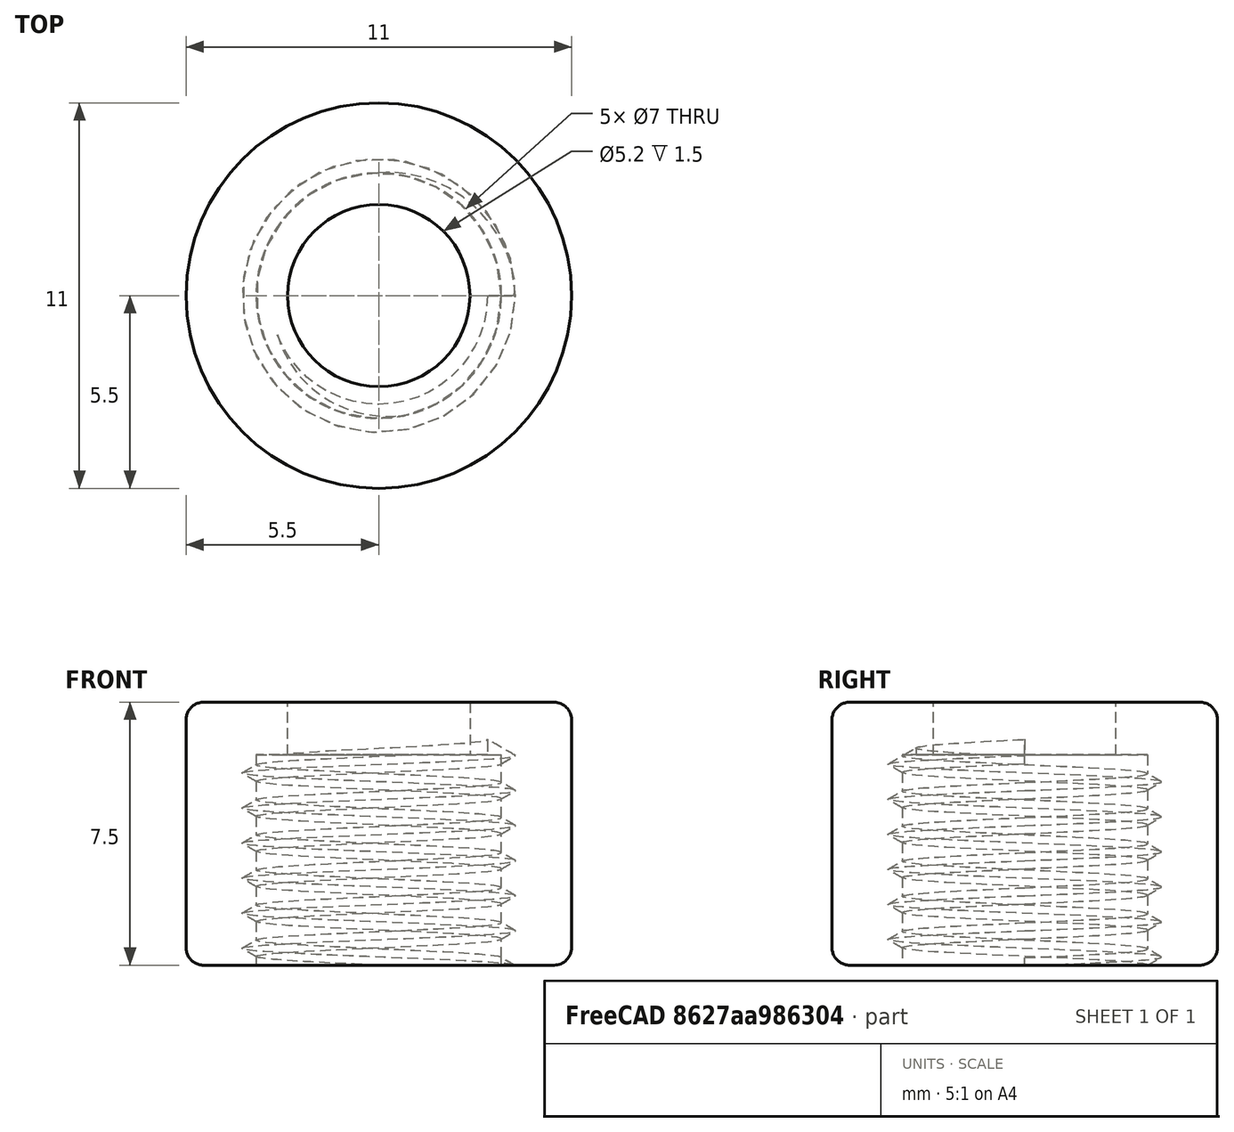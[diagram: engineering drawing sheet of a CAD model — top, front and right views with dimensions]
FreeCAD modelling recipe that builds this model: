
FCSTD DOCUMENT  (FreeCAD 0.19R24291 (Git))
Label: soldernut
License: All rights reserved
LicenseURL: http://en.wikipedia.org/wiki/All_rights_reserved
objects: TechDraw::DrawViewDimension×7, Sketcher::SketchObject×4, TechDraw::DrawProjGroupItem×4, Part::Extrusion×3, Part::Cut×3, Part::Fillet×2, Part::Helix×1, PartDesign::Body×1, Part::Sweep×1, TechDraw::DrawSVGTemplate×1, TechDraw::DrawProjGroup×1, TechDraw::DrawViewSection×1, TechDraw::DrawPage×1
note: 15 computed .brp shape members not serialized (recipe doc carries the construction recipe); baked Part::Feature solids carry a one-line shape summary decoded from their .brp

FEATURE [Sketcher::SketchObject] Sketch
  FullyConstrained = true
  Placement = pos=(0,0,0) rot=(1,0,0;3.14159rad)
  sketch-geometry (1):
    g0: Circle CenterX=0 CenterY=0 CenterZ=0 NormalX=0 NormalY=0 NormalZ=1 AngleXU=0 Radius=5.5
  constraints (2):
    c: Coincident(g0,g-1)
    c: Radius(g0) = 5.5  'внешний контур'
FEATURE [Part::Extrusion] Extrude
  Base = -> Sketch
  Dir = (0,0,-1)
  DirMode = 2
  FaceMakerClass = Part::FaceMakerBullseye
  LengthFwd = 7.5
  LengthRev = 0
  Solid = true
  Symmetric = false
FEATURE [Sketcher::SketchObject] Sketch001
  FullyConstrained = true
  MapMode = 5
  Placement = pos=(0,0,-7.5) rot=(1,0,0;3.14159rad)
  Support = -> [Extrude]
  sketch-geometry (1):
    g0: Circle CenterX=0 CenterY=0 CenterZ=0 NormalX=0 NormalY=0 NormalZ=1 AngleXU=0 Radius=3.5
  constraints (2):
    c: Coincident(g0,g-1)
    c: Radius(g0) = 3.5  'Внутренний больший радиус'
FEATURE [Part::Extrusion] Extrude001
  Base = -> Sketch001
  Dir = (0,0,-1)
  DirMode = 2
  FaceMakerClass = Part::FaceMakerBullseye
  LengthFwd = -6
  LengthRev = 0
  Solid = true
  Symmetric = false
FEATURE [Part::Cut] Cut
  Base = -> Extrude
  Tool = -> Extrude001
FEATURE [Sketcher::SketchObject] Sketch002
  FullyConstrained = true
  MapMode = 5
  Support = -> [Cut]
  sketch-geometry (1):
    g0: Circle CenterX=0 CenterY=0 CenterZ=0 NormalX=0 NormalY=0 NormalZ=1 AngleXU=0 Radius=2.6
  constraints (2):
    c: Coincident(g0,g-1)
    c: Radius(g0) = 2.6
FEATURE [Part::Extrusion] Extrude002
  Base = -> Sketch002
  Dir = (0,0,1)
  DirMode = 2
  FaceMakerClass = Part::FaceMakerBullseye
  LengthFwd = -8
  LengthRev = 0
  Solid = true
  Symmetric = false
FEATURE [Part::Cut] Cut001
  Base = -> Cut
  Tool = -> Extrude002
FEATURE [Part::Fillet] Fillet
  Base = -> Cut001
  Edges = 1 edges r=0.5: [Edge2]
FEATURE [Part::Fillet] Fillet001
  Base = -> Fillet
  Edges = 1 edges r=0.5: [Edge2]
FEATURE [Part::Helix] Helix  label="Спираль"
  Angle = 0
  AttacherType = Attacher::AttachEngine3D
  Height = 6
  LocalCoord = 0
  Pitch = 1
  Placement = pos=(0,0,-7.5) rot=(0,0,1;0rad)
  Radius = 3.5
  Style = 1
FEATURE [Sketcher::SketchObject] Sketch003
  FullyConstrained = true
  MapMode = 5
  Placement = pos=(0,0,0) rot=(1,0,0;1.5708rad)
  Support = -> [XZ_Plane]
  sketch-geometry (3):
    g0: LineSegment StartX=3.9 StartY=-7.52 StartZ=0 EndX=3.1 EndY=-7.05812 EndZ=0
    g1: LineSegment StartX=3.1 StartY=-7.05812 StartZ=0 EndX=3.1 EndY=-7.98188 EndZ=0
    g2: LineSegment StartX=3.1 StartY=-7.98188 StartZ=0 EndX=3.9 EndY=-7.52 EndZ=0
  constraints (9):
    c: Coincident(g0,g1)
    c: Vertical(g1)
    c: Coincident(g1,g2)
    c: Coincident(g2,g0)
    c: Equal(g0,g2)
    c: Angle(g0,g2) = 1.0472
    c: DistanceX(g-1,g0) = 3.9
    c: DistanceY(g0,g-1) = 7.52
    c: DistanceX(g-1,g1) = 3.1
FEATURE [PartDesign::Body] Body
  Group = -> [Sketch003]
  Origin = -> Origin
FEATURE [Part::Sweep] Sweep
  Frenet = true
  Sections = -> [Sketch003]
  Solid = true
  Spine = -> Helix [Edge1,Edge2,Edge3,Edge4,Edge5,Edge6]
  Transition = 1
FEATURE [Part::Cut] Cut002
  Base = -> Fillet001
  Tool = -> Sweep
FEATURE [TechDraw::DrawSVGTemplate] Template
  Height = 297
  Orientation = 1
  Width = 420
FEATURE [TechDraw::DrawProjGroupItem] ProjItem  label="Front"
  CoarseView = false
  Direction = (0,-1,0)
  Focus = 100
  HardHidden = false
  IsoCount = 0
  IsoHidden = false
  IsoVisible = false
  LockPosition = true
  Perspective = false
  Rotation = 0
  RotationVector = (1,0,0)
  Scale = 6
  ScaleType = 2
  SeamHidden = false
  SeamVisible = true
  SmoothHidden = false
  SmoothVisible = true
  Source = -> [Cut002]
  Type = 0
  X = 0
  XDirection = (1,0,0)
  Y = 0
FEATURE [TechDraw::DrawProjGroupItem] ProjItem001  label="Bottom"
  CoarseView = false
  Direction = (0,0,-1)
  Focus = 100
  HardHidden = false
  IsoCount = 0
  IsoHidden = false
  IsoVisible = false
  LockPosition = false
  Perspective = false
  Rotation = 0
  RotationVector = (1,0,0)
  Scale = 6
  ScaleType = 2
  SeamHidden = false
  SeamVisible = true
  SmoothHidden = false
  SmoothVisible = true
  Source = -> [Cut002]
  Type = 5
  X = 0
  XDirection = (1,0,0)
  Y = 85.9201
FEATURE [TechDraw::DrawProjGroupItem] ProjItem002  label="Top"
  CoarseView = false
  Direction = (0,0,1)
  Focus = 100
  HardHidden = false
  IsoCount = 0
  IsoHidden = false
  IsoVisible = false
  LockPosition = false
  Perspective = false
  Rotation = 0
  RotationVector = (1,0,0)
  Scale = 6
  ScaleType = 2
  SeamHidden = false
  SeamVisible = true
  SmoothHidden = false
  SmoothVisible = true
  Source = -> [Cut002]
  Type = 4
  X = 0
  XDirection = (1,0,0)
  Y = -89.9779
FEATURE [TechDraw::DrawProjGroupItem] ProjItem003  label="FrontBottomLeft"
  CoarseView = false
  Direction = (-0.57735,-0.57735,-0.57735)
  Focus = 100
  HardHidden = false
  IsoCount = 0
  IsoHidden = false
  IsoVisible = false
  LockPosition = false
  Perspective = false
  Rotation = 0
  RotationVector = (1,0,0)
  Scale = 6
  ScaleType = 2
  SeamHidden = false
  SeamVisible = true
  SmoothHidden = false
  SmoothVisible = true
  Source = -> [Cut002]
  Type = 8
  X = 84.7919
  XDirection = (0.707107,-0.707107,0)
  Y = 89.4829
FEATURE [TechDraw::DrawProjGroup] ProjGroup
  Anchor = -> ProjItem
  AutoDistribute = true
  LockPosition = false
  ProjectionType = 0
  Rotation = 0
  Scale = 6
  ScaleType = 2
  Source = -> [Cut002]
  Views = -> [ProjItem,ProjItem001,ProjItem002,ProjItem003]
  X = 72.5645
  Y = 156.996
  spacingX = 15
  spacingY = 15
FEATURE [TechDraw::DrawViewSection] SectionView  label="Section  - "
  BaseView = -> ProjItem
  CoarseView = false
  CutSurfaceDisplay = 2
  Direction = (-1,0,0)
  FileGeomPattern = C:/Program Files/FreeCAD 0.19/data/Mod/TechDraw/PAT/FCPAT.pat
  FileHatchPattern = C:/Program Files/FreeCAD 0.19/data/Mod/TechDraw/Patterns/simple.svg
  Focus = 100
  FuseBeforeCut = false
  HardHidden = false
  HatchScale = 1
  IsoCount = 0
  IsoHidden = false
  IsoVisible = false
  LockPosition = false
  NameGeomPattern = Diamond
  Perspective = false
  Rotation = 0
  Scale = 15
  ScaleType = 0
  SeamHidden = false
  SeamVisible = true
  SectionDirection = 0
  SectionNormal = (-1,0,0)
  SectionOrigin = (-0.16,0,-3.99)
  SmoothHidden = false
  SmoothVisible = true
  Source = -> [Cut002]
  X = 282.206
  XDirection = (0,-1,0)
  Y = 97.5996
FEATURE [TechDraw::DrawViewDimension] Dimension
  Arbitrary = false
  ArbitraryTolerances = false
  EqualTolerance = true
  FormatSpec = %.2f
  FormatSpecOverTolerance = %+.2f
  FormatSpecUnderTolerance = %+.2f
  Inverted = false
  LockPosition = false
  MeasureType = 1
  OverTolerance = 0
  References2D = -> [SectionView]
  Rotation = 0
  ScaleType = 0
  TheoreticalExact = false
  Type = 2
  UnderTolerance = 0
  X = 102.838
  Y = 6.94587
FEATURE [TechDraw::DrawViewDimension] Dimension001
  Arbitrary = false
  ArbitraryTolerances = false
  EqualTolerance = true
  FormatSpec = %.2f
  FormatSpecOverTolerance = %+.2f
  FormatSpecUnderTolerance = %+.2f
  Inverted = false
  LockPosition = false
  MeasureType = 1
  OverTolerance = 0
  References2D = -> [SectionView]
  Rotation = 0
  ScaleType = 0
  TheoreticalExact = false
  Type = 1
  UnderTolerance = 0
  X = 2.07363
  Y = 92.7618
FEATURE [TechDraw::DrawViewDimension] Dimension002
  Arbitrary = false
  ArbitraryTolerances = false
  EqualTolerance = true
  FormatSpec = %.2f
  FormatSpecOverTolerance = %+.2f
  FormatSpecUnderTolerance = %+.2f
  Inverted = false
  LockPosition = false
  MeasureType = 1
  OverTolerance = 0
  References2D = -> [SectionView]
  Rotation = 0
  ScaleType = 0
  TheoreticalExact = false
  Type = 1
  UnderTolerance = 0
  X = 1.66588
  Y = 77.3453
FEATURE [TechDraw::DrawViewDimension] Dimension003
  Arbitrary = false
  ArbitraryTolerances = false
  EqualTolerance = true
  FormatSpec = R%.2f
  FormatSpecOverTolerance = %+.2f
  FormatSpecUnderTolerance = %+.2f
  Inverted = false
  LockPosition = false
  MeasureType = 1
  OverTolerance = 0
  References2D = -> [SectionView]
  Rotation = 0
  ScaleType = 0
  TheoreticalExact = false
  Type = 4
  UnderTolerance = 0
  X = -96.2048
  Y = 76.2142
FEATURE [TechDraw::DrawViewDimension] Dimension004
  Arbitrary = false
  ArbitraryTolerances = false
  EqualTolerance = true
  FormatSpec = %.2f
  FormatSpecOverTolerance = %+.2f
  FormatSpecUnderTolerance = %+.2f
  Inverted = false
  LockPosition = false
  MeasureType = 1
  OverTolerance = 0
  References2D = -> [SectionView]
  Rotation = 0
  ScaleType = 0
  TheoreticalExact = false
  Type = 2
  UnderTolerance = 0
  X = -108.893
  Y = 46.1153
FEATURE [TechDraw::DrawViewDimension] Dimension005
  Arbitrary = false
  ArbitraryTolerances = false
  EqualTolerance = true
  FormatSpec = %.2f
  FormatSpecOverTolerance = %+.2f
  FormatSpecUnderTolerance = %+.2f
  Inverted = false
  LockPosition = false
  MeasureType = 1
  OverTolerance = 0
  References2D = -> [SectionView]
  Rotation = 0
  ScaleType = 0
  TheoreticalExact = false
  Type = 2
  UnderTolerance = 0
  X = -108.712
  Y = -7.6359
FEATURE [TechDraw::DrawViewDimension] Dimension006
  Arbitrary = false
  ArbitraryTolerances = false
  EqualTolerance = true
  FormatSpec = %.2f
  FormatSpecOverTolerance = %+.2f
  FormatSpecUnderTolerance = %+.2f
  Inverted = false
  LockPosition = false
  MeasureType = 1
  OverTolerance = 0
  References2D = -> [SectionView]
  Rotation = 0
  ScaleType = 0
  TheoreticalExact = false
  Type = 1
  UnderTolerance = 0
  X = -0.416471
  Y = -65.963
FEATURE [TechDraw::DrawPage] Page
  KeepUpdated = true
  NextBalloonIndex = 1
  ProjectionType = 0
  Template = -> Template
  Views = -> [ProjGroup,SectionView,Dimension,Dimension001,Dimension002,Dimension003,Dimension004,Dimension005,Dimension006]
